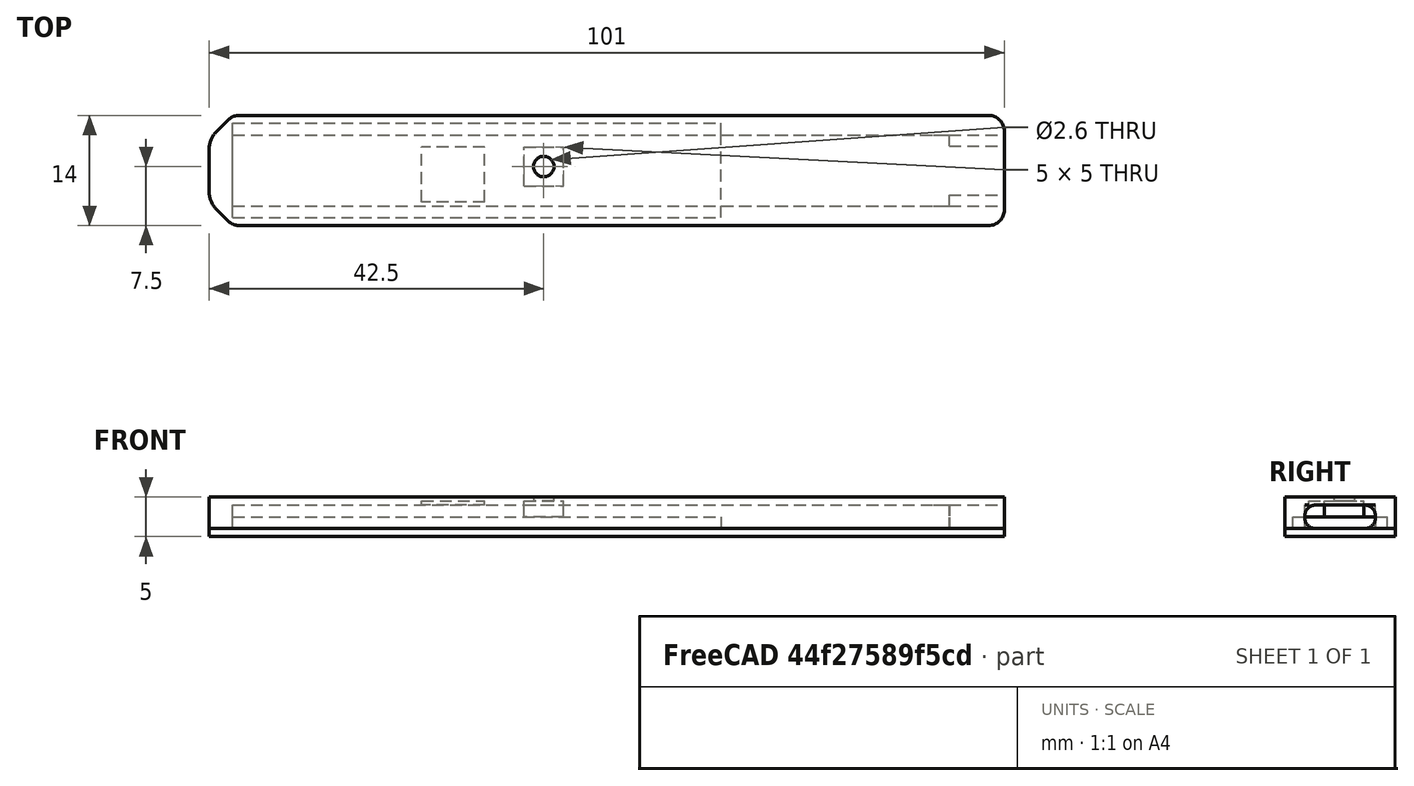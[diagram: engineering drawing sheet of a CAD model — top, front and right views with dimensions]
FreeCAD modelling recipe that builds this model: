
FCSTD DOCUMENT  (FreeCAD 0.20R29603 (Git))
Label: box_for_device
License: All rights reserved
LicenseURL: http://en.wikipedia.org/wiki/All_rights_reserved
objects: Part::Fillet×11, Part::Box×10, Part::Cut×6, Part::Chamfer×4, Part::MultiFuse×2, Part::Cylinder×1
note: 34 computed .brp shape members not serialized (recipe doc carries the construction recipe); baked Part::Feature solids carry a one-line shape summary decoded from their .brp

FEATURE [Part::Box] Box  label="Куб"
  AttacherType = Attacher::AttachEngine3D
  Height = 1.5
  Length = 62
  Width = 12
FEATURE [Part::Box] Box001  label="Куб001"
  AttacherType = Attacher::AttachEngine3D
  Height = 3
  Length = 5
  Placement = pos=(37,4,0) rot=(0,0,1;0rad)
  Width = 5
FEATURE [Part::MultiFuse] Fusion
  Shapes = -> [Box,Box001]
FEATURE [Part::Box] Box002  label="Куб002"
  AttacherType = Attacher::AttachEngine3D
  Height = 4
  Length = 101
  Placement = pos=(-3,-1,0) rot=(0,0,1;0rad)
  Width = 14
FEATURE [Part::Box] Box003  label="Куб003"
  AttacherType = Attacher::AttachEngine3D
  Height = 3
  Length = 91
  Placement = pos=(0,1.5,0) rot=(0,0,1;0rad)
  Width = 9
FEATURE [Part::Cut] Cut
  Base = -> Box002
  Tool = -> Box003
FEATURE [Part::Box] Box004  label="Куб004"
  AttacherType = Attacher::AttachEngine3D
  Height = 1.5
  Length = 62
  Width = 12
FEATURE [Part::Box] Box005  label="Куб005"
  AttacherType = Attacher::AttachEngine3D
  Height = 3
  Length = 5
  Placement = pos=(37,4,0) rot=(0,0,1;0rad)
  Width = 5
FEATURE [Part::MultiFuse] Fusion001
  Shapes = -> [Box004,Box005]
FEATURE [Part::Cut] Cut001
  Base = -> Cut
  Tool = -> Fusion001
FEATURE [Part::Box] Box006  label="Куб006"
  AttacherType = Attacher::AttachEngine3D
  Height = 3
  Length = 9
  Width = 9
FEATURE [Part::Fillet] Fillet
  Base = -> Box006
  Edges = 2 edges r=1.4: [Edge11,Edge12]
FEATURE [Part::Fillet] Fillet001
  Base = -> Fillet
  Edges = 2 edges r=1.4: [Edge7,Edge12]
  Placement = pos=(89,1.5,0) rot=(0,0,1;0rad)
FEATURE [Part::Cut] Cut002
  Base = -> Cut001
  Tool = -> Fillet001
FEATURE [Part::Fillet] Fillet002
  Base = -> Cut002
  Edges = 1 edges r=2: [Edge6]
FEATURE [Part::Fillet] Fillet003
  Base = -> Fillet002
  Edges = 1 edges r=2: [Edge36]
FEATURE [Part::Chamfer] Chamfer
  Base = -> Fillet003
  Edges = 1 edges r=3: [Edge38]
FEATURE [Part::Chamfer] Chamfer001
  Base = -> Chamfer
  Edges = 1 edges r=3: [Edge24]
FEATURE [Part::Fillet] Fillet004
  Base = -> Chamfer001
  Edges = 1 edges r=2: [Edge29]
FEATURE [Part::Fillet] Fillet005
  Base = -> Fillet004
  Edges = 1 edges r=2: [Edge34]
FEATURE [Part::Box] Box007  label="Куб007"
  AttacherType = Attacher::AttachEngine3D
  Height = 1
  Length = 101
  Placement = pos=(-3,-1,-1) rot=(0,0,1;0rad)
  Width = 14
FEATURE [Part::Fillet] Fillet006
  Base = -> Box007
  Edges = 2 edges r=2: [Edge5,Edge7]
FEATURE [Part::Chamfer] Chamfer002
  Base = -> Fillet006
  Edges = 1 edges r=3: [Edge17]
FEATURE [Part::Chamfer] Chamfer003
  Base = -> Chamfer002
  Edges = 1 edges r=3: [Edge15]
FEATURE [Part::Fillet] Fillet007
  Base = -> Chamfer003
  Edges = 1 edges r=2: [Edge13]
FEATURE [Part::Fillet] Fillet008
  Base = -> Fillet007
  Edges = 1 edges r=2: [Edge20]
FEATURE [Part::Fillet] Fillet009
  Base = -> Fillet005
  Edges = 2 edges r=3: [Edge32,Edge44]
FEATURE [Part::Fillet] Fillet010
  Base = -> Fillet008
  Edges = 2 edges r=3: [Edge19,Edge22]
FEATURE [Part::Cylinder] Cylinder  label="Цилиндр"
  Angle = 360
  AttacherType = Attacher::AttachEngine3D
  FirstAngle = 0
  Height = 10
  Placement = pos=(39.5,6.5,0) rot=(0,0,1;0rad)
  Radius = 1.3
  SecondAngle = 0
FEATURE [Part::Cut] Cut003
  Base = -> Fillet009
  Tool = -> Cylinder
FEATURE [Part::Box] Box008  label="Куб008"
  AttacherType = Attacher::AttachEngine3D
  Height = 10
  Length = 5
  Placement = pos=(37,4,-6.5) rot=(0,0,1;0rad)
  Width = 5
FEATURE [Part::Cut] Cut004
  Base = -> Cut003
  Tool = -> Box008
FEATURE [Part::Box] Box009  label="Куб009"
  AttacherType = Attacher::AttachEngine3D
  Height = 9
  Length = 8
  Placement = pos=(24,2,-5.5) rot=(0,0,1;0rad)
  Width = 7
FEATURE [Part::Cut] Cut005
  Base = -> Cut004
  Tool = -> Box009
